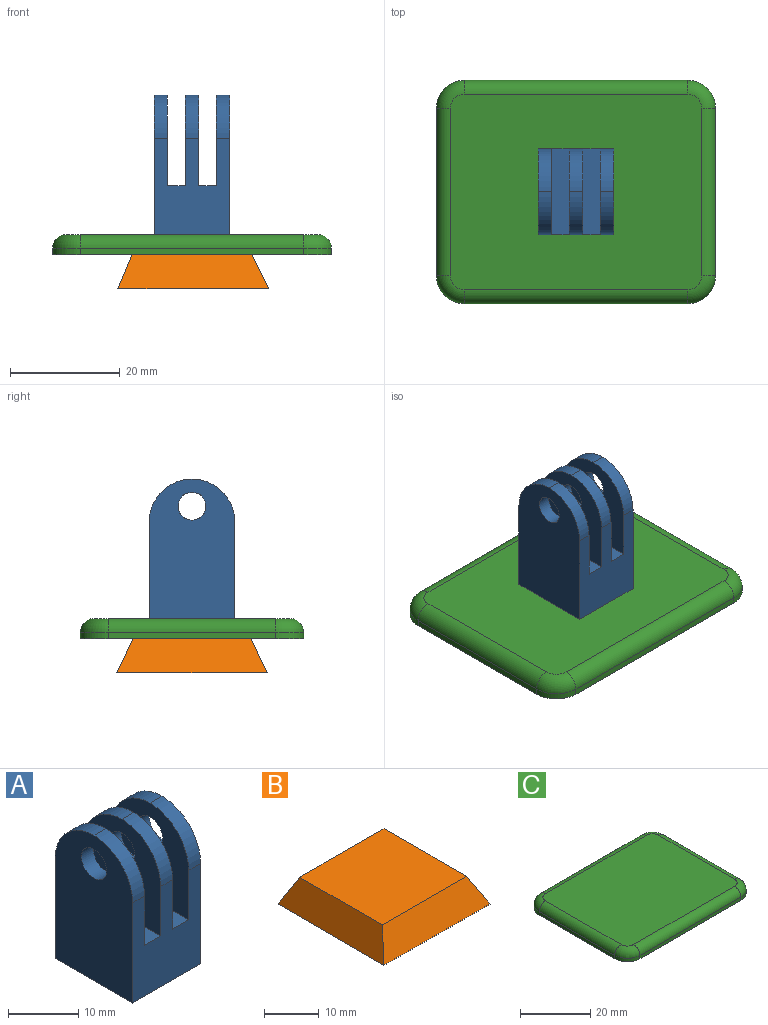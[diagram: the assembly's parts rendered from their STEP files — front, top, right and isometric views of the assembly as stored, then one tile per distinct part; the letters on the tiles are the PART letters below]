
ASSEMBLY  parts=3 mates=2
PART A: 20 faces, bbox 13.7x15.6x25.4 mm
  f0: plane 15.62x13.75mm, normal (0,0,-1), area 214.8mm2, adj f1,f2,f3,f10
  f1: plane 25.4x15.62mm, normal (-1,0,0), area 349.9mm2, adj f0,f2,f3,f15,f16,f19
  f2: plane 17.53x13.75mm, normal (0,1,0), area 184.8mm2, adj f0,f1,f4,f5,f6,f7,f8,f9
  f3: plane 17.53x13.75mm, normal (0,-1,0), area 184.8mm2, adj f0,f1,f4,f5,f6,f7,f8,f9
  f4: plane 16.51x15.62mm, normal (1,0,0), area 211mm2, adj f2,f3,f6,f15,f16,f19
  f5: plane 16.51x15.62mm, normal (-1,0,0), area 211mm2, adj f2,f3,f6,f13,f14,f18
  f6: plane 15.62x3.25mm, normal (0,0,1), area 50.8mm2, adj f2,f3,f4,f5
  f7: plane 16.51x15.62mm, normal (1,0,0), area 211mm2, adj f2,f3,f9,f13,f14,f18
  f8: plane 16.51x15.62mm, normal (-1,0,0), area 211mm2, adj f2,f3,f9,f11,f12,f17
  f9: plane 15.62x3.25mm, normal (0,0,1), area 50.8mm2, adj f2,f3,f7,f8
  f10: plane 25.4x15.62mm, normal (1,0,0), area 349.9mm2, adj f0,f2,f3,f11,f12,f17
  f11: cylinder r=7.87mm len=7.87mm, axis (-1,0,0), area 29.8mm2, adj f3,f8,f10,f12
  f12: cylinder r=7.87mm len=7.87mm, axis (1,0,0), area 29.8mm2, adj f2,f8,f10,f11
  f13: cylinder r=7.87mm len=7.87mm, axis (-1,0,0), area 29.7mm2, adj f3,f5,f7,f14
  f14: cylinder r=7.87mm len=7.87mm, axis (1,0,0), area 29.7mm2, adj f2,f5,f7,f13
  f15: cylinder r=7.87mm len=7.87mm, axis (1,0,0), area 29.7mm2, adj f1,f2,f4,f16
  f16: cylinder r=7.87mm len=7.87mm, axis (-1,0,0), area 29.7mm2, adj f1,f3,f4,f15
  f17: cylinder r=2.54mm len=5.08mm, axis (1,0,0), area 38.6mm2, adj f8,f10
  f18: cylinder r=2.54mm len=5.08mm, axis (1,0,0), area 38.5mm2, adj f5,f7
  f19: cylinder r=2.54mm len=5.08mm, axis (1,0,0), area 38.5mm2, adj f1,f4
PART B: 11 faces, bbox 27.4x27.4x6.2 mm
  f0: plane 27.43x27.43mm, normal (0,0,-1), area 258.6mm2, adj f2,f3,f4,f5,f6,f7,f8,f9
  f1: plane 21.78x21.34mm, normal (0,0,1), area 464.7mm2, adj f2,f3,f4,f5
  f2: plane 27.43x6.22mm, normal (0,-0.9,0.44), area 170.5mm2, adj f0,f1,f4,f5
  f3: plane 27.43x6.22mm, normal (0,0.9,0.44), area 170.5mm2, adj f0,f1,f4,f5
  f4: plane 27.43x6.22mm, normal (-0.92,0,0.39), area 164.5mm2, adj f0,f1,f2,f3
  f5: plane 27.43x6.22mm, normal (0.9,0,0.44), area 169mm2, adj f0,f1,f2,f3
  f6: plane 22.23x4.32mm, normal (0,1,0), area 96mm2, adj f0,f7,f9,f10
  f7: plane 22.23x4.32mm, normal (1,0,0), area 96mm2, adj f0,f6,f8,f10
  f8: plane 22.23x4.32mm, normal (0,-1,0), area 96mm2, adj f0,f7,f9,f10
  f9: plane 22.23x4.32mm, normal (-1,0,0), area 96mm2, adj f0,f6,f8,f10
  f10: plane 22.23x22.23mm, normal (0,0,-1), area 494mm2, adj f6,f7,f8,f9
PART C: 18 faces, bbox 51.6x41.5x3.7 mm
  f0: plane 40.64x1.14mm, normal (0,1,0), area 46.5mm2, adj f4,f6,f9,f17
  f1: plane 30.48x1.14mm, normal (-1,0,0), area 34.8mm2, adj f4,f6,f7,f13
  f2: plane 40.64x1.14mm, normal (0,-1,0), area 46.5mm2, adj f4,f7,f8,f10
  f3: plane 30.48x1.14mm, normal (1,0,0), area 34.8mm2, adj f4,f8,f9,f14
  f4: plane 50.8x40.64mm, normal (0,0,-1), area 2042.4mm2, adj f0,f1,f2,f3,f6,f7,f8,f9
  f5: plane 45.72x35.56mm, normal (0,0,1), area 1620.3mm2, adj f10,f11,f12,f13,f14,f15,f16,f17
  f6: cylinder r=5.08mm len=5.08mm, axis (0,0,-1), area 9.1mm2, adj f0,f1,f4,f15
  f7: cylinder r=5.08mm len=5.08mm, axis (0,0,1), area 9.1mm2, adj f1,f2,f4,f11
  f8: cylinder r=5.08mm len=5.08mm, axis (0,0,-1), area 9.1mm2, adj f2,f3,f4,f12
  f9: cylinder r=5.08mm len=5.08mm, axis (0,0,1), area 9.1mm2, adj f0,f3,f4,f16
  f10: cylinder r=2.54mm len=40.64mm, axis (1,0,0), area 162.1mm2, adj f2,f5,f11,f12
  f11: torus R=2.54mm, axis (0,0,1), area 26.1mm2, adj f5,f7,f10,f13
  f12: torus R=2.54mm, axis (0,0,1), area 26.1mm2, adj f5,f8,f10,f14
  f13: cylinder r=2.54mm len=30.48mm, axis (0,-1,0), area 121.6mm2, adj f1,f5,f11,f15
  f14: cylinder r=2.54mm len=30.48mm, axis (0,1,0), area 121.6mm2, adj f3,f5,f12,f16
  f15: torus R=2.54mm, axis (0,0,1), area 26.1mm2, adj f5,f6,f13,f17
  f16: torus R=2.54mm, axis (0,0,1), area 26.1mm2, adj f5,f9,f14,f17
  f17: cylinder r=2.54mm len=40.64mm, axis (-1,0,0), area 162.1mm2, adj f0,f5,f15,f16
PLACE A t=(2.46,2.52,18.87)mm
PLACE B t=(1.81,10.33,2.49)mm
PLACE C t=(2.03,10.33,6.17)mm
MATE fastened C.f4 <-> B.f1  axis (0,0,-1) through (2.03,10.33,2.49)mm
MATE fastened C.f5 <-> A.f0  axis (0,0,1) through (2.03,10.33,6.17)mm
